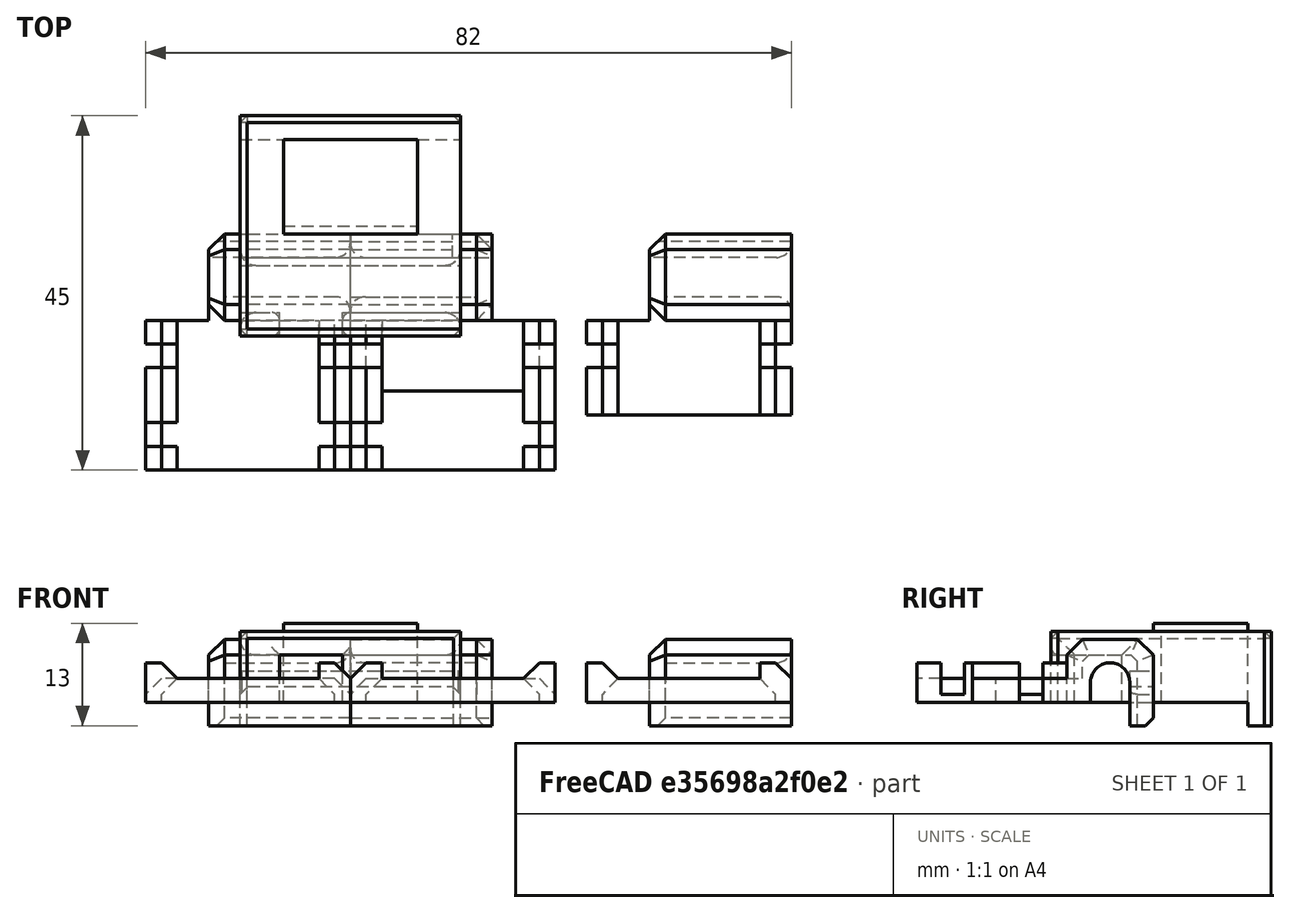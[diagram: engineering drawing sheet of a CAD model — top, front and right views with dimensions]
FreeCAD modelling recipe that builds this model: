
FCSTD DOCUMENT  (FreeCAD 0.18R14555 (Git shallow))
Label: X-moto-wire-holder
License: All rights reserved
LicenseURL: http://en.wikipedia.org/wiki/All_rights_reserved
objects: Part::Box×25, Part::Chamfer×12, Part::Cut×7, Part::MultiFuse×6, Part::Feature×6, Part::Fillet×3, Part::Cylinder×1, Part::Mirroring×1
note: 61 computed .brp shape members not serialized (recipe doc carries the construction recipe); baked Part::Feature solids carry a one-line shape summary decoded from their .brp

FEATURE [Part::Box] Box  label="Cube"
  AttacherType = Attacher::AttachEngine3D
  Height = 11
  Length = 18
  Placement = pos=(0,-3,-3) rot=(0,0,1;0rad)
  Width = 3
FEATURE [Part::Box] Box001  label="Cube001"
  AttacherType = Attacher::AttachEngine3D
  Height = 8
  Length = 18
  Placement = pos=(0,-11,0) rot=(0,0,1;0rad)
  Width = 11
FEATURE [Part::Box] Box002  label="Cube002"
  AttacherType = Attacher::AttachEngine3D
  Height = 8
  Length = 18
  Placement = pos=(0,-11,0) rot=(0,0,1;0rad)
  Width = 3
FEATURE [Part::Box] Box003  label="Cube003"
  AttacherType = Attacher::AttachEngine3D
  Height = 3
  Length = 26
  Placement = pos=(0,-20,0) rot=(0,0,1;0rad)
  Width = 17
FEATURE [Part::Cylinder] Cylinder
  Angle = 360
  AttacherType = Attacher::AttachEngine3D
  Height = 16
  Placement = pos=(16,-5.5,2.5) rot=(0,-1,0;1.5708rad)
  Radius = 2.5
FEATURE [Part::Box] Box004  label="Cube004"
  AttacherType = Attacher::AttachEngine3D
  Height = 2.5
  Length = 16
  Placement = pos=(0,-8,0) rot=(0,0,1;0rad)
  Width = 5
FEATURE [Part::MultiFuse] Fusion
  Shapes = -> [Box004,Cylinder]
FEATURE [Part::MultiFuse] Fusion001
  Shapes = -> [Box003,Box,Box001,Box002]
FEATURE [Part::Cut] Cut
  Base = -> Fusion001
  Tool = -> Fusion
FEATURE [Part::Chamfer] Chamfer
  Base = -> Cut
  Edges = 2 edges r=2: [Edge23,Edge62]
FEATURE [Part::Chamfer] Chamfer001
  Base = -> Chamfer
  Edges = 1 edges r=1: [Edge80]
FEATURE [Part::Box] Box005  label="Cube005"
  AttacherType = Attacher::AttachEngine3D
  Height = 10
  Length = 10
  Placement = pos=(18,-11,0) rot=(0,0,1;0rad)
  Width = 10
FEATURE [Part::Cut] Cut001
  Base = -> Chamfer001
  Tool = -> Box005
FEATURE [Part::Feature] Cut001001  label="Cut002"
  shape: bbox 26 x 20 x 11 mm, 18 faces (baked)
FEATURE [Part::Box] Box006  label="Cube006"
  AttacherType = Attacher::AttachEngine3D
  Height = 3
  Length = 2
  Placement = pos=(0,-17,0) rot=(0,0,1;0rad)
  Width = 3
FEATURE [Part::Box] Box007  label="Cube007"
  AttacherType = Attacher::AttachEngine3D
  Height = 3
  Length = 2
  Placement = pos=(24,-17,0) rot=(0,0,1;0rad)
  Width = 3
FEATURE [Part::MultiFuse] Fusion002
  Shapes = -> [Box007,Box006]
FEATURE [Part::Cut] Cut001002
  Base = -> Cut001001
  Tool = -> Fusion002
FEATURE [Part::Chamfer] Chamfer002
  Base = -> Cut001002
  Edges = 2 edges r=2: [Edge35,Edge40]
FEATURE [Part::Box] Box008  label="Cube008"
  AttacherType = Attacher::AttachEngine3D
  Height = 5
  Length = 4
  Placement = pos=(0,-20,0) rot=(0,0,1;0rad)
  Width = 3
FEATURE [Part::Box] Box009  label="Cube009"
  AttacherType = Attacher::AttachEngine3D
  Height = 5
  Length = 4
  Placement = pos=(0,-14,0) rot=(0,0,1;0rad)
  Width = 3
FEATURE [Part::Box] Box010  label="Cube010"
  AttacherType = Attacher::AttachEngine3D
  Height = 5
  Length = 4
  Placement = pos=(22,-14,0) rot=(0,0,1;0rad)
  Width = 3
FEATURE [Part::Box] Box011  label="Cube011"
  AttacherType = Attacher::AttachEngine3D
  Height = 5
  Length = 4
  Placement = pos=(22,-20,0) rot=(0,0,1;0rad)
  Width = 3
FEATURE [Part::Chamfer] Chamfer003
  Base = -> Box011
  Edges = 1 edges r=2: [Edge2]
FEATURE [Part::Chamfer] Chamfer004
  Base = -> Box010
  Edges = 1 edges r=2: [Edge2]
FEATURE [Part::Chamfer] Chamfer005
  Base = -> Box008
  Edges = 1 edges r=2: [Edge2]
FEATURE [Part::Chamfer] Chamfer006
  Base = -> Box009
  Edges = 1 edges r=2: [Edge2]
FEATURE [Part::Fillet] Fillet
  Base = -> Chamfer002
  Edges = 4 edges r=1.9: [Edge39,Edge41,Edge42,Edge44]
FEATURE [Part::Chamfer] Chamfer007
  Base = -> Fillet
  Edges = 5 edges r=2: [Edge57,Edge62,Edge65,Edge70,Edge74]
FEATURE [Part::Box] Box012  label="Cube012"
  AttacherType = Attacher::AttachEngine3D
  Height = 3
  Length = 26
  Placement = pos=(0,-30,0) rot=(0,0,1;0rad)
  Width = 10
FEATURE [Part::Chamfer] Chamfer008
  Base = -> Box012
  Edges = 2 edges r=2: [Edge2,Edge6]
FEATURE [Part::Feature] Fusion003001  label="Fusion004"
  Placement = pos=(0,-10,0) rot=(0,0,1;0rad)
  shape: bbox 26 x 9 x 5 mm, 28 faces, 4 solids (baked)
FEATURE [Part::MultiFuse] Fusion003002
  Shapes = -> [Chamfer003,Chamfer005]
FEATURE [Part::Feature] Fusion003002001  label="Fusion003003"
  Placement = pos=(0,-2,0) rot=(0,0,1;0rad)
  shape: bbox 26 x 3 x 5 mm, 14 faces, 2 solids (baked)
FEATURE [Part::MultiFuse] Fusion003002002
  Shapes = -> [Chamfer004,Fusion003002,Fusion003002001,Chamfer006,Fusion003001,Chamfer008,Chamfer007]
FEATURE [Part::Feature] Fusion003002002001  label="Fusion003002003"
  shape: bbox 26 x 30 x 11 mm, 60 faces (baked)
FEATURE [Part::Mirroring] Part__Mirroring  label="Fusion003002003 (Mirror #1)"
  Base = (0,0,0)
  Normal = (1,0,0)
  Source = -> Fusion003002002001
FEATURE [Part::Feature] Part__Mirroring001  label="Fusion003002003 (Mirror #1)001"
  shape: bbox 26 x 30 x 11 mm, 60 faces (baked)
FEATURE [Part::Box] Box013  label="Cube013"
  AttacherType = Attacher::AttachEngine3D
  Height = 10
  Length = 30
  Placement = pos=(-28,-34,0) rot=(0,0,1;0rad)
  Width = 11
FEATURE [Part::Cut] Cut001003
  Base = -> Part__Mirroring001
  Placement = pos=(56,0,0) rot=(0,0,1;0rad)
  Tool = -> Box013
FEATURE [Part::Box] Box014  label="wire-tab"
  AttacherType = Attacher::AttachEngine3D
  Height = 10
  Length = 17
  Placement = pos=(-8.5,0,0) rot=(0,0,1;0rad)
  Width = 12
FEATURE [Part::Box] Box015  label="Cube014"
  AttacherType = Attacher::AttachEngine3D
  Height = 9
  Length = 5.5
  Placement = pos=(8.5,1,0) rot=(0,0,1;0rad)
  Width = 11
FEATURE [Part::Box] Box016  label="Cube015"
  AttacherType = Attacher::AttachEngine3D
  Height = 9
  Length = 5.5
  Placement = pos=(-14,1,0) rot=(0,0,1;0rad)
  Width = 11
FEATURE [Part::Box] Box017  label="Cube016"
  AttacherType = Attacher::AttachEngine3D
  Height = 12
  Length = 28
  Placement = pos=(-14,12,-3) rot=(0,0,1;0rad)
  Width = 3
FEATURE [Part::Box] Box018  label="Cube017"
  AttacherType = Attacher::AttachEngine3D
  Height = 2
  Length = 28
  Placement = pos=(-14,-3,2) rot=(0,0,1;0rad)
  Width = 3
FEATURE [Part::Box] Box019  label="Cube018"
  AttacherType = Attacher::AttachEngine3D
  Height = 3
  Length = 28
  Placement = pos=(-14,-13,6) rot=(0,0,1;0rad)
  Width = 9
FEATURE [Part::Box] Box020  label="Cube019"
  AttacherType = Attacher::AttachEngine3D
  Height = 6
  Length = 5
  Placement = pos=(-14,-13,0) rot=(0,0,1;0rad)
  Width = 3
FEATURE [Part::Box] Box021  label="Cube020"
  AttacherType = Attacher::AttachEngine3D
  Height = 6
  Length = 15
  Placement = pos=(-1,-13,0) rot=(0,0,1;0rad)
  Width = 3
FEATURE [Part::Box] Box022  label="Cube021"
  AttacherType = Attacher::AttachEngine3D
  Height = 9
  Length = 28
  Placement = pos=(-14,-4,0) rot=(0,0,1;0rad)
  Width = 5
FEATURE [Part::MultiFuse] Fusion003002002002
  Shapes = -> [Box017,Box015,Box016,Box022,Box019,Box021,Box020]
FEATURE [Part::Feature] Fusion003002002002001  label="Fusion003002002003"
  shape: bbox 28 x 28 x 12 mm, 19 faces (baked)
FEATURE [Part::Fillet] Fillet001
  Base = -> Fusion003002002002001
  Edges = 6 edges r=2: [Edge24,Edge25,Edge26,Edge30,Edge33,Edge40]
FEATURE [Part::Cut] Cut001004
  Base = -> Fillet001
  Tool = -> Box018
FEATURE [Part::Fillet] Fillet002
  Base = -> Cut001004
  Edges = 5 edges r=1: [Edge38,Edge39,Edge43,Edge80,Edge84]
FEATURE [Part::Chamfer] Chamfer009
  Base = -> Fillet002
  Edges = 7 edges r=0.9: [Edge3,Edge5,Edge7,Edge18,Edge31,Edge32,Edge42]
FEATURE [Part::Box] Box023  label="Cube022"
  AttacherType = Attacher::AttachEngine3D
  Height = 2
  Length = 3
  Placement = pos=(16,-3,0) rot=(0,0,1;0rad)
  Width = 3
FEATURE [Part::Box] Box024  label="Cube023"
  AttacherType = Attacher::AttachEngine3D
  Height = 2
  Length = 3
  Placement = pos=(-18,-3,0) rot=(0,0,1;0rad)
  Width = 3
FEATURE [Part::Chamfer] Chamfer010
  Base = -> Box023
  Edges = 1 edges r=1: [Edge4]
  Placement = pos=(-3,0,1) rot=(0,0,1;0rad)
FEATURE [Part::Cut] Cut001005
  Base = -> Chamfer009
  Tool = -> Chamfer010
FEATURE [Part::Chamfer] Chamfer011
  Base = -> Box024
  Edges = 1 edges r=1: [Edge8]
  Placement = pos=(2,0,1) rot=(0,0,1;0rad)
FEATURE [Part::Cut] Cut001006
  Base = -> Cut001005
  Tool = -> Chamfer011
